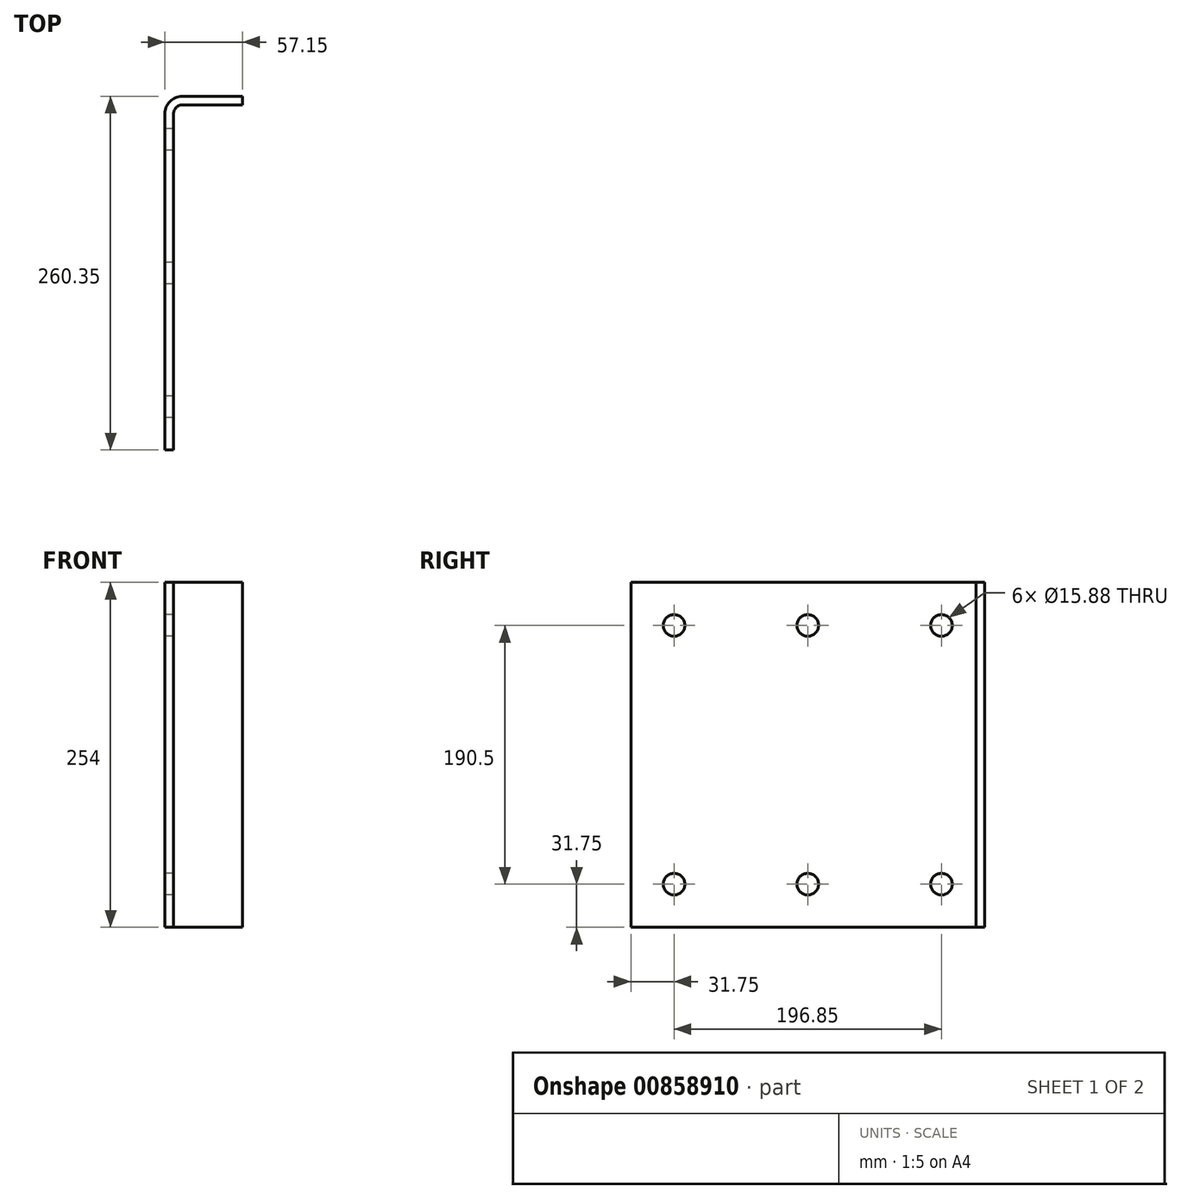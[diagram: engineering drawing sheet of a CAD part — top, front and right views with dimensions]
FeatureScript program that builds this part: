
annotation { "Feature Type Name" : "Feature", "Feature Type Description" : "" }
export const myFeature = defineFeature(function(context is Context, id is Id, definition is map)
    precondition{}
    {
        {
            var Q0;
            Q0=qCreatedBy(makeId("Top.planeOp"),FACE);
            var sketch = newSketch(context, id + "F0", { "sketchPlane" : qUnion([Q0])});
            skLineSegment(sketch, "E0", {"start": v(0, 0) * mm, "end": v(0, 247.65) * mm});
            skLineSegment(sketch, "E1", {"start": v(6.35, 254) * mm, "end": v(50.8, 254) * mm});
            skPoint(sketch, "E2.visualSharp", {"position": v(0, 254) * mm});
            skArc(sketch, "E2.filletArc", {"start": v(6.35, 254) * mm, "mid": v(1.86, 252.14) * mm, "end": v(0, 247.65) * mm});
            skLineSegment(sketch, "E3.0", {"start": v(6.35, 260.35) * mm, "end": v(50.8, 260.35) * mm});
            skArc(sketch, "E3.1", {"start": v(6.35, 260.35) * mm, "mid": v(-2.63, 256.63) * mm, "end": v(-6.35, 247.65) * mm});
            skLineSegment(sketch, "E3.2", {"start": v(-6.35, 0) * mm, "end": v(-6.35, 247.65) * mm});
            skLineSegment(sketch, "E4", {"start": v(-6.35, 0) * mm, "end": v(0, 0) * mm});
            skLineSegment(sketch, "E5", {"start": v(50.8, 260.35) * mm, "end": v(50.8, 254) * mm});
            skSolve(sketch);
        }
        {
            var Q0;
            Q0 = qSketchRegion(id + "F0", true);
            extrude(context, id + "F1", {"entities" : qUnion([Q0]), "depth" : 254 * mm, "offsetDistance" : 25.4 * mm});
        }
        {
            var Q0;
            Q0=makeQuery(id+"F1.opExtrude","SWEPT_FACE",FACE,{"disambiguationData":[OSD([sQuery(id+"F0.wireOp",EDGE,"E3.2")])]});
            var sketch = newSketch(context, id + "F2", { "sketchPlane" : qUnion([Q0])});
            skLineSegment(sketch, "E6.0", {"start": v(0, 0) * mm, "end": v(-260.35, 0) * mm, "construction": true});
            skLineSegment(sketch, "E7.0", {"start": v(0, 254) * mm, "end": v(0, 0) * mm, "construction": true});
            skLineSegment(sketch, "E8.0", {"start": v(0, 254) * mm, "end": v(-260.35, 254) * mm, "construction": true});
            skLineSegment(sketch, "E9.0", {"start": v(-260.35, 254) * mm, "end": v(-260.35, 0) * mm, "construction": true});
            skPoint(sketch, "E10.orphan", {"position": v(-247.65, 0) * mm});
            skPoint(sketch, "E11.orphan", {"position": v(-247.65, 254) * mm});
            skLineSegment(sketch, "E12.0", {"start": v(-31.75, 31.75) * mm, "end": v(-228.6, 31.75) * mm, "construction": true});
            skLineSegment(sketch, "E12.1", {"start": v(-31.75, 222.25) * mm, "end": v(-31.75, 31.75) * mm, "construction": true});
            skLineSegment(sketch, "E12.2", {"start": v(-31.75, 222.25) * mm, "end": v(-228.6, 222.25) * mm, "construction": true});
            skLineSegment(sketch, "E12.3", {"start": v(-228.6, 222.25) * mm, "end": v(-228.6, 31.75) * mm, "construction": true});
            skLineSegment(sketch, "E13", {"start": v(-31.75, 127) * mm, "end": v(-228.6, 127) * mm, "construction": true});
            skLineSegment(sketch, "E14", {"start": v(-130.17, 222.25) * mm, "end": v(-130.17, 31.75) * mm, "construction": true});
            skCircle(sketch, "E15", {"center": v(-228.6, 31.75) * mm, "radius": 7.94 * mm});
            skCircle(sketch, "E16", {"center": v(-228.6, 222.25) * mm, "radius": 7.94 * mm});
            skCircle(sketch, "E17", {"center": v(-130.17, 222.25) * mm, "radius": 7.94 * mm});
            skCircle(sketch, "E18", {"center": v(-130.17, 31.75) * mm, "radius": 7.94 * mm});
            skCircle(sketch, "E19", {"center": v(-31.75, 31.75) * mm, "radius": 7.94 * mm});
            skCircle(sketch, "E20", {"center": v(-31.75, 222.25) * mm, "radius": 7.94 * mm});
            skSolve(sketch);
        }
        {
            var Q0;
            Q0 = qSketchRegion(id + "F2", true);
            extrude(context, id + "F3", {"entities" : qUnion([Q0]), "operationType" : NewBodyOperationType.REMOVE, "oppositeDirection" : true, "depth" : 25.4 * mm, "offsetDistance" : 25.4 * mm});
        }
    });
